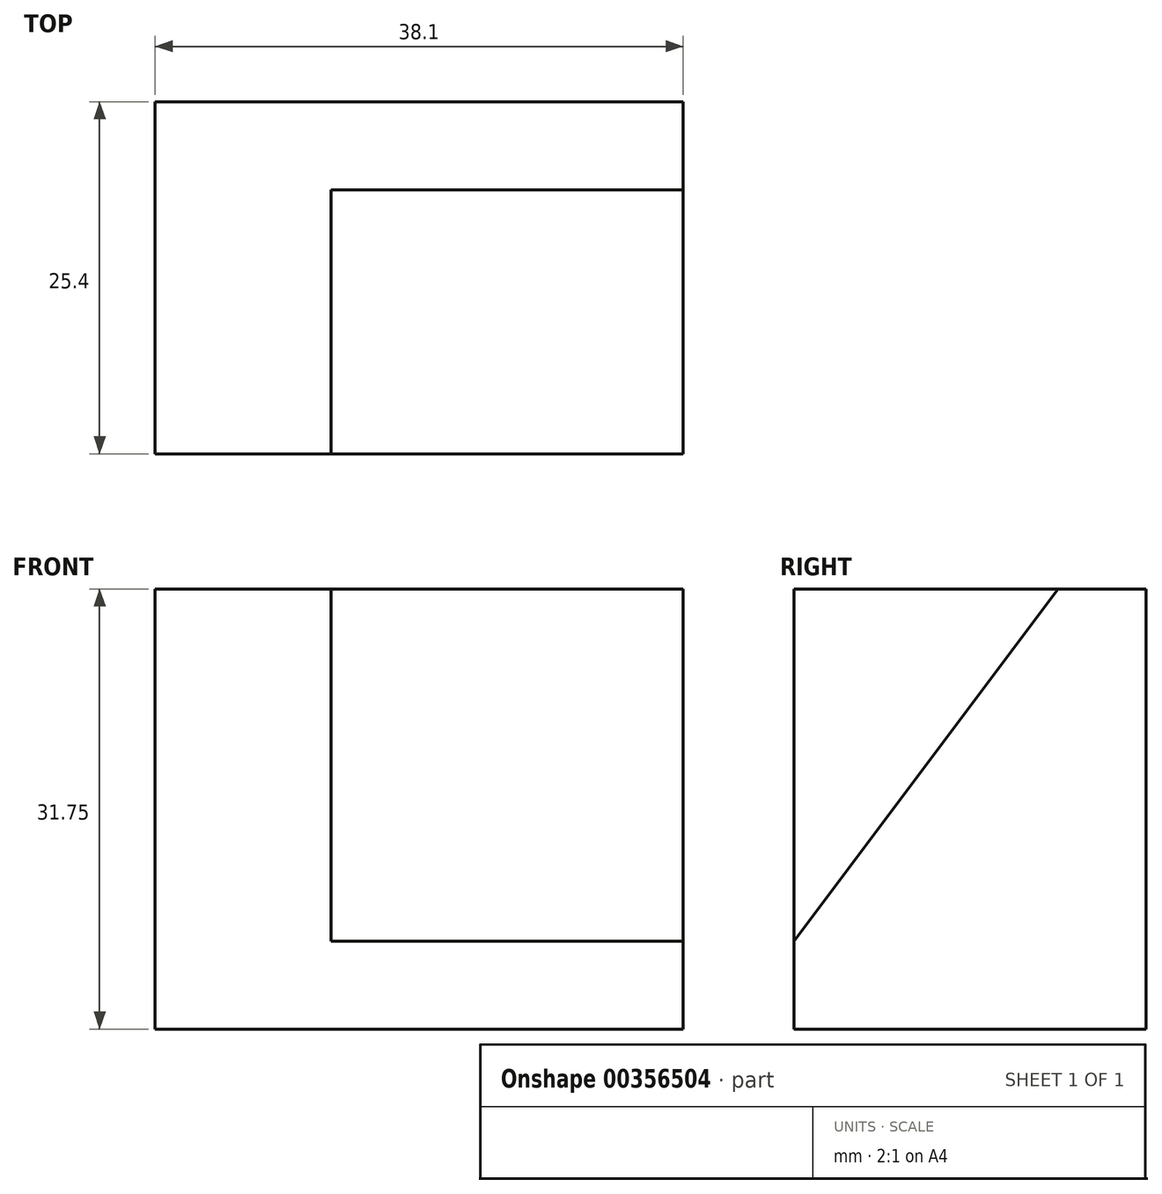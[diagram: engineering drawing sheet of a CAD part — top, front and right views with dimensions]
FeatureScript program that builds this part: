
annotation { "Feature Type Name" : "Feature", "Feature Type Description" : "" }
export const myFeature = defineFeature(function(context is Context, id is Id, definition is map)
    precondition{}
    {
        {
            var Q0;
            Q0=qCreatedBy(makeId("Right.planeOp"),FACE);
            var sketch = newSketch(context, id + "F0", { "sketchPlane" : qUnion([Q0])});
            skLineSegment(sketch, "E0", {"start": v(0, 0) * mm, "end": v(0, 31.75) * mm});
            skLineSegment(sketch, "E1", {"start": v(0, 31.75) * mm, "end": v(25.4, 31.75) * mm});
            skLineSegment(sketch, "E2", {"start": v(25.4, 31.75) * mm, "end": v(25.4, 0) * mm});
            skLineSegment(sketch, "E3", {"start": v(25.4, 0) * mm, "end": v(0, 0) * mm});
            skSolve(sketch);
        }
        {
            var Q0;
            Q0=makeQuery(id+"F0.imprint","IMPRINT",FACE,{"disambiguationData":[TD([[makeQuery(id+"F0.imprint","IMPRINT",EDGE,{"derivedFrom":sQuery(id+"F0.wireOp",EDGE,"E0")}),-1.0]])]});
            extrude(context, id + "F1", {"entities" : qUnion([Q0]), "oppositeDirection" : true, "depth" : 38.1 * mm});
        }
        {
            var Q0;
            Q0=makeQuery(id+"F1.opExtrude","CAP_FACE",FACE,{"disambiguationData":[OSD([sQuery(id+"F0.wireOp",EDGE,"E0"),sQuery(id+"F0.wireOp",EDGE,"E1"),sQuery(id+"F0.wireOp",EDGE,"E2"),sQuery(id+"F0.wireOp",EDGE,"E3")])],"isStart":true});
            var sketch = newSketch(context, id + "F2", { "sketchPlane" : qUnion([Q0])});
            skLineSegment(sketch, "E4", {"start": v(0, 31.75) * mm, "end": v(19.05, 31.75) * mm});
            skLineSegment(sketch, "E5", {"start": v(19.05, 31.75) * mm, "end": v(0, 6.35) * mm});
            skLineSegment(sketch, "E6", {"start": v(0, 6.35) * mm, "end": v(0, 31.75) * mm});
            skSolve(sketch);
        }
        {
            var Q0;
            Q0=makeQuery(id+"F2.imprint","IMPRINT",FACE,{"disambiguationData":[TD([[makeQuery(id+"F2.imprint","IMPRINT",EDGE,{"derivedFrom":sQuery(id+"F2.wireOp",EDGE,"E4")}),-1.0]])]});
            extrude(context, id + "F3", {"entities" : qUnion([Q0]), "operationType" : NewBodyOperationType.REMOVE, "oppositeDirection" : true, "depth" : 25.4 * mm});
        }
    });
